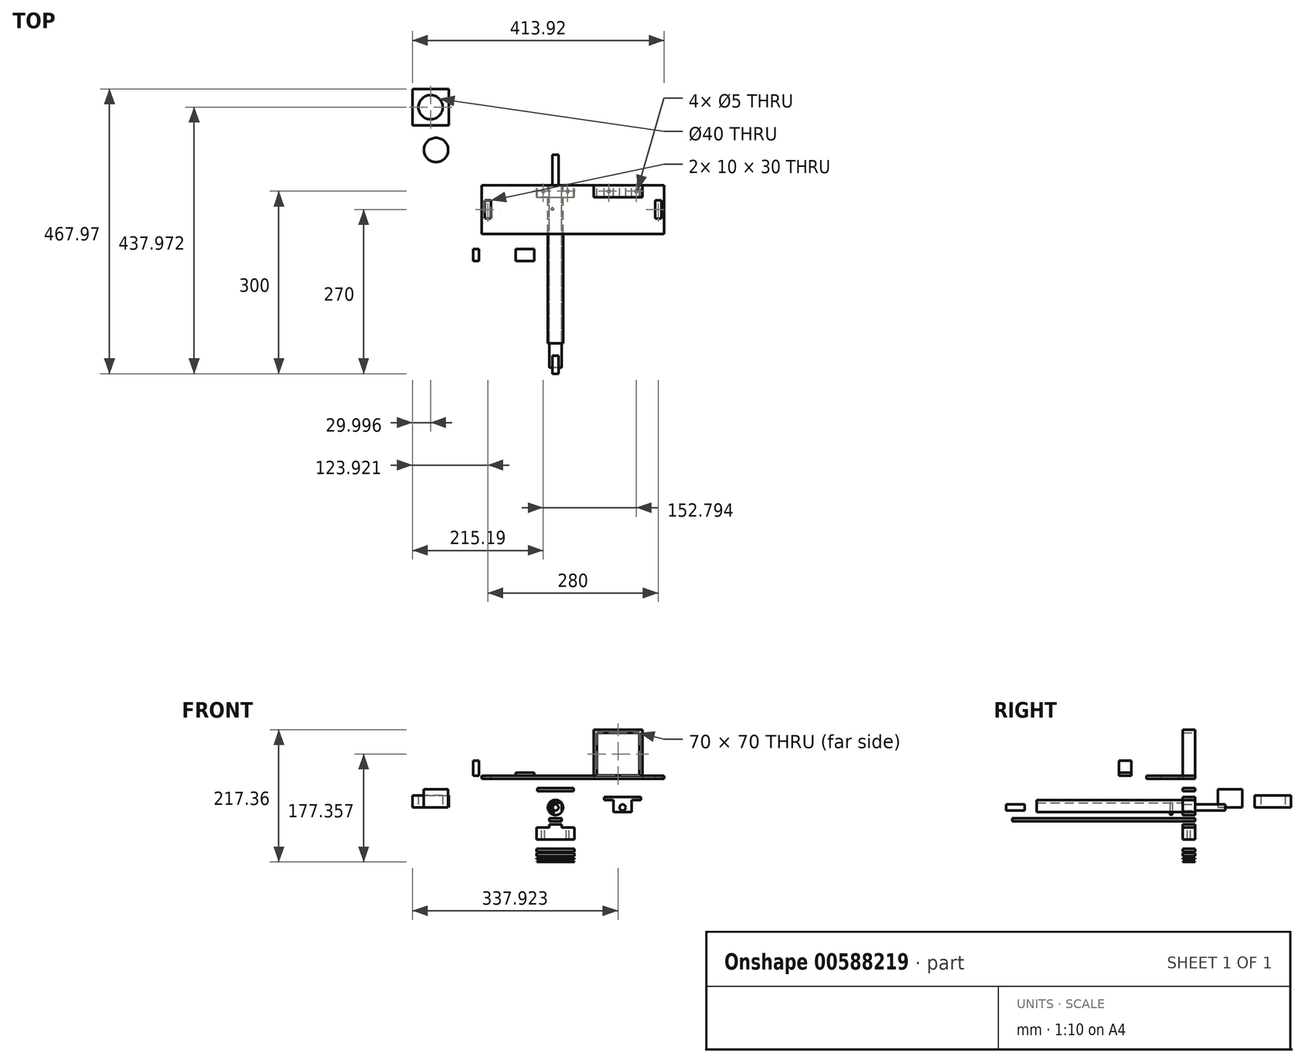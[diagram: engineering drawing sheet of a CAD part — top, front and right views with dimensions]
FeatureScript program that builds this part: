
annotation { "Feature Type Name" : "Feature", "Feature Type Description" : "" }
export const myFeature = defineFeature(function(context is Context, id is Id, definition is map)
    precondition{}
    {
        {
            var Q0;
            Q0=qCreatedBy(makeId("Front.planeOp"),FACE);
            var sketch = newSketch(context, id + "F0", { "sketchPlane" : qUnion([Q0])});
            skCircle(sketch, "E0", {"center": v(0, 0) * mm, "radius": 12.5 * mm});
            skCircle(sketch, "E1", {"center": v(110.3, 0) * mm, "radius": 5 * mm});
            skLineSegment(sketch, "E2.bottom", {"start": v(-30, 31.74) * mm, "end": v(30, 31.74) * mm});
            skLineSegment(sketch, "E2.top", {"start": v(-30, 26.74) * mm, "end": v(30, 26.74) * mm});
            skLineSegment(sketch, "E2.left", {"start": v(-30, 31.74) * mm, "end": v(-30, 26.74) * mm});
            skLineSegment(sketch, "E2.right", {"start": v(30, 31.74) * mm, "end": v(30, 26.74) * mm});
            skPoint(sketch, "E2.middle", {"position": v(0, 29.24) * mm});
            skLineSegment(sketch, "E3", {"start": v(110.3, 10) * mm, "end": v(110.3, -10) * mm, "construction": true});
            skCircle(sketch, "E4", {"center": v(110.3, 0) * mm, "radius": 12.5 * mm, "construction": true});
            skLineSegment(sketch, "E5", {"start": v(97.8, 0) * mm, "end": v(122.8, 0) * mm, "construction": true});
            skLineSegment(sketch, "E6", {"start": v(110.3, 12.5) * mm, "end": v(79.29, 12.5) * mm, "construction": true});
            skLineSegment(sketch, "E7", {"start": v(110.3, 5) * mm, "end": v(79.29, 5) * mm, "construction": true});
            skLineSegment(sketch, "E8", {"start": v(110.3, -5) * mm, "end": v(79.29, -5) * mm, "construction": true});
            skLineSegment(sketch, "E9", {"start": v(110.3, -12.5) * mm, "end": v(79.29, -12.5) * mm, "construction": true});
            skLineSegment(sketch, "E10", {"start": v(110.3, -7.5) * mm, "end": v(125.3, -7.5) * mm});
            skLineSegment(sketch, "E11", {"start": v(110.3, 17.5) * mm, "end": v(140.3, 17.5) * mm});
            skLineSegment(sketch, "E12", {"start": v(125.3, 12.5) * mm, "end": v(140.3, 12.5) * mm});
            skLineSegment(sketch, "E13", {"start": v(125.3, -7.5) * mm, "end": v(125.3, 12.5) * mm});
            skLineSegment(sketch, "E14", {"start": v(140.3, 17.5) * mm, "end": v(140.3, 12.5) * mm});
            skPoint(sketch, "E15.orphan", {"position": v(110.3, 12.5) * mm});
            skLineSegment(sketch, "E16.MirrorCS", {"start": v(95.3, 12.5) * mm, "end": v(80.3, 12.5) * mm});
            skLineSegment(sketch, "E17.MirrorCS", {"start": v(80.3, 17.5) * mm, "end": v(80.3, 12.5) * mm});
            skLineSegment(sketch, "E18.MirrorCS", {"start": v(110.3, 17.5) * mm, "end": v(80.3, 17.5) * mm});
            skLineSegment(sketch, "E19.MirrorCS", {"start": v(95.3, -7.5) * mm, "end": v(95.3, 12.5) * mm});
            skLineSegment(sketch, "E20.MirrorCS", {"start": v(110.3, -7.5) * mm, "end": v(95.3, -7.5) * mm});
            skLineSegment(sketch, "E21.top", {"start": v(0, -27.58) * mm, "end": v(10, -27.58) * mm});
            skLineSegment(sketch, "E22", {"start": v(10.93, -32.58) * mm, "end": v(30.93, -32.58) * mm});
            skLineSegment(sketch, "E23", {"start": v(30.93, -32.58) * mm, "end": v(30.93, -52.58) * mm});
            skLineSegment(sketch, "E24", {"start": v(30.93, -52.58) * mm, "end": v(0, -52.58) * mm});
            skLineSegment(sketch, "E25.MirrorCS", {"start": v(0, -27.58) * mm, "end": v(-10, -27.58) * mm});
            skLineSegment(sketch, "E26.MirrorCS", {"start": v(-10.93, -32.58) * mm, "end": v(-30.93, -32.58) * mm});
            skLineSegment(sketch, "E27.MirrorCS", {"start": v(-30.93, -32.58) * mm, "end": v(-30.93, -52.58) * mm});
            skLineSegment(sketch, "E28.MirrorCS", {"start": v(-30.93, -52.58) * mm, "end": v(0, -52.58) * mm});
            skLineSegment(sketch, "E29", {"start": v(0, -22.52) * mm, "end": v(10, -22.52) * mm});
            skLineSegment(sketch, "E30", {"start": v(10, -22.52) * mm, "end": v(10, -17.52) * mm});
            skLineSegment(sketch, "E31", {"start": v(10, -17.52) * mm, "end": v(0, -17.52) * mm});
            skLineSegment(sketch, "E32.MirrorCS", {"start": v(-10, -17.52) * mm, "end": v(0, -17.52) * mm});
            skLineSegment(sketch, "E33.MirrorCS", {"start": v(0, -22.52) * mm, "end": v(-10, -22.52) * mm});
            skLineSegment(sketch, "E34.MirrorCS", {"start": v(-10, -22.52) * mm, "end": v(-10, -17.52) * mm});
            skLineSegment(sketch, "E35.bottom", {"start": v(137.73, 52.7) * mm, "end": v(67.73, 52.7) * mm});
            skLineSegment(sketch, "E35.top", {"start": v(137.73, 122.7) * mm, "end": v(67.73, 122.7) * mm});
            skLineSegment(sketch, "E35.left", {"start": v(137.73, 52.7) * mm, "end": v(137.73, 122.7) * mm});
            skLineSegment(sketch, "E35.right", {"start": v(67.73, 52.7) * mm, "end": v(67.73, 122.7) * mm});
            skPoint(sketch, "E35.middle", {"position": v(102.73, 87.7) * mm});
            skLineSegment(sketch, "E36.bottom", {"start": v(62.73, 127.7) * mm, "end": v(142.73, 127.7) * mm});
            skLineSegment(sketch, "E36.top", {"start": v(62.73, 47.7) * mm, "end": v(142.73, 47.7) * mm});
            skLineSegment(sketch, "E36.left", {"start": v(62.73, 127.7) * mm, "end": v(62.73, 47.7) * mm});
            skLineSegment(sketch, "E36.right", {"start": v(142.73, 127.7) * mm, "end": v(142.73, 47.7) * mm});
            skLineSegment(sketch, "E37.bottom", {"start": v(-30.93, -79.86) * mm, "end": v(30.93, -79.86) * mm});
            skLineSegment(sketch, "E37.top", {"start": v(-30.93, -74.86) * mm, "end": v(30.93, -74.86) * mm});
            skLineSegment(sketch, "E37.left", {"start": v(-30.93, -79.86) * mm, "end": v(-30.93, -74.86) * mm});
            skLineSegment(sketch, "E37.right", {"start": v(30.93, -79.86) * mm, "end": v(30.93, -74.86) * mm});
            skLineSegment(sketch, "E38.MirrorCS", {"start": v(-30.74, -88.65) * mm, "end": v(31.12, -88.65) * mm});
            skLineSegment(sketch, "E39.MirrorCS", {"start": v(-30.74, -89.65) * mm, "end": v(31.12, -89.65) * mm});
            skLineSegment(sketch, "E40", {"start": v(-30.93, -82.76) * mm, "end": v(30.93, -82.76) * mm});
            skLineSegment(sketch, "E41", {"start": v(30.93, -82.76) * mm, "end": v(30.93, -84.76) * mm});
            skLineSegment(sketch, "E42", {"start": v(30.93, -84.76) * mm, "end": v(-30.93, -84.76) * mm});
            skLineSegment(sketch, "E43", {"start": v(-30.93, -84.76) * mm, "end": v(-30.93, -82.76) * mm});
            skLineSegment(sketch, "E44", {"start": v(-30.74, -88.65) * mm, "end": v(-30.74, -89.65) * mm});
            skLineSegment(sketch, "E45", {"start": v(31.12, -88.65) * mm, "end": v(31.12, -89.65) * mm});
            skLineSegment(sketch, "E46", {"start": v(-30.93, -72.74) * mm, "end": v(30.93, -72.74) * mm});
            skLineSegment(sketch, "E47", {"start": v(30.93, -72.74) * mm, "end": v(30.93, -67.74) * mm});
            skLineSegment(sketch, "E48", {"start": v(30.93, -67.74) * mm, "end": v(-30.93, -67.74) * mm});
            skLineSegment(sketch, "E49", {"start": v(-30.93, -67.74) * mm, "end": v(-30.93, -72.74) * mm});
            skLineSegment(sketch, "E50", {"start": v(-10, -27.58) * mm, "end": v(-10, -32.58) * mm});
            skLineSegment(sketch, "E51", {"start": v(-10, -32.58) * mm, "end": v(-10.93, -32.58) * mm});
            skPoint(sketch, "E52.MirrorCS.end.orphan", {"position": v(-10, -27.58) * mm});
            skPoint(sketch, "E52.MirrorCS.start.orphan", {"position": v(-10.93, -32.58) * mm});
            skLineSegment(sketch, "E53", {"start": v(10, -27.58) * mm, "end": v(10, -32.58) * mm});
            skLineSegment(sketch, "E54", {"start": v(10, -32.58) * mm, "end": v(10.93, -32.58) * mm});
            skLineSegment(sketch, "E55.left", {"start": v(194.47, 95.4) * mm, "end": v(194.47, 97.9) * mm});
            skLineSegment(sketch, "E56.bottom", {"start": v(-122.7, 157) * mm, "end": v(-422.7, 157) * mm});
            skLineSegment(sketch, "E56.top", {"start": v(-122.7, 159.5) * mm, "end": v(-422.7, 159.5) * mm});
            skLineSegment(sketch, "E56.left", {"start": v(-122.7, 157) * mm, "end": v(-122.7, 159.5) * mm});
            skLineSegment(sketch, "E56.right", {"start": v(-422.7, 157) * mm, "end": v(-422.7, 159.5) * mm});
            skLineSegment(sketch, "E57", {"start": v(-272.7, 150) * mm, "end": v(-272.7, 153.49) * mm, "construction": true});
            skPoint(sketch, "E57.startSnap0", {"position": v(-272.7, 157) * mm});
            skSolve(sketch);
        }
        {
            var Q0;
            Q0=makeQuery(id+"F0.imprint","IMPRINT",FACE,{"disambiguationData":[TD([[makeQuery(id+"F0.imprint","IMPRINT",EDGE,{"derivedFrom":sQuery(id+"F0.wireOp",EDGE,"E1")}),-1.0]])]});
            var Q1;
            Q1=makeQuery(id+"F0.imprint","IMPRINT",FACE,{"disambiguationData":[TD([[makeQuery(id+"F0.imprint","IMPRINT",EDGE,{"derivedFrom":sQuery(id+"F0.wireOp",EDGE,"E2.bottom")}),-1.0]])]});
            var Q2;
            Q2=makeQuery(id+"F0.imprint","IMPRINT",FACE,{"disambiguationData":[TD([[makeQuery(id+"F0.imprint","IMPRINT",EDGE,{"derivedFrom":sQuery(id+"F0.wireOp",EDGE,"E21.top")}),-1.0]])]});
            var Q3;
            Q3=makeQuery(id+"F0.imprint","IMPRINT",FACE,{"disambiguationData":[TD([[makeQuery(id+"F0.imprint","IMPRINT",EDGE,{"derivedFrom":sQuery(id+"F0.wireOp",EDGE,"E35.bottom")}),1.0]])]});
            var Q4;
            Q4=makeQuery(id+"F0.imprint","IMPRINT",FACE,{"disambiguationData":[TD([[makeQuery(id+"F0.imprint","IMPRINT",EDGE,{"derivedFrom":sQuery(id+"F0.wireOp",EDGE,"E37.bottom")}),1.0]])]});
            var Q5;
            Q5=makeQuery(id+"F0.imprint","IMPRINT",FACE,{"disambiguationData":[TD([[makeQuery(id+"F0.imprint","IMPRINT",EDGE,{"derivedFrom":sQuery(id+"F0.wireOp",EDGE,"E38.MirrorCS")}),-1.0]])]});
            var Q6;
            Q6=makeQuery(id+"F0.imprint","IMPRINT",FACE,{"disambiguationData":[TD([[makeQuery(id+"F0.imprint","IMPRINT",EDGE,{"derivedFrom":sQuery(id+"F0.wireOp",EDGE,"E40")}),-1.0]])]});
            var Q7;
            Q7=makeQuery(id+"F0.imprint","IMPRINT",FACE,{"disambiguationData":[TD([[makeQuery(id+"F0.imprint","IMPRINT",EDGE,{"derivedFrom":sQuery(id+"F0.wireOp",EDGE,"E46")}),1.0]])]});
            var Q8;
            {var subQ5=sQuery(id+"F0.wireOp",EDGE,"E55.right");Q8=makeQuery(id+"F0.imprint","IMPRINT",FACE,{"disambiguationData":[TD([[makeQuery(id+"F0.imprint","IMPRINT",EDGE,{"derivedFrom":subQ5}),-1.0]])]});}
            extrude(context, id + "F1", {"entities" : qUnion([Q0, Q1, Q2, Q3, Q4, Q5, Q6, Q7, Q8]), "depth" : 20 * mm, "offsetDistance" : 25 * mm});
        }
        {
            var Q0;
            Q0=makeQuery(id+"F0.imprint","IMPRINT",FACE,{"disambiguationData":[TD([[makeQuery(id+"F0.imprint","IMPRINT",EDGE,{"derivedFrom":sQuery(id+"F0.wireOp",EDGE,"E0")}),1.0]])]});
            extrude(context, id + "F2", {"entities" : qUnion([Q0]), "depth" : 260 * mm, "offsetDistance" : 25 * mm});
        }
        {
            var Q0;
            Q0=makeQuery(id+"F2.opExtrude","CAP_FACE",FACE,{"disambiguationData":[OSD([sQuery(id+"F0.wireOp",EDGE,"E0")])],"isStart":false});
            var sketch = newSketch(context, id + "F3", { "sketchPlane" : qUnion([Q0])});
            skCircle(sketch, "E58", {"center": v(0, 0) * mm, "radius": 5 * mm});
            skSolve(sketch);
        }
        {
            var Q0;
            Q0=makeQuery(id+"F3.imprint","IMPRINT",FACE,{"disambiguationData":[TD([[makeQuery(id+"F3.imprint","IMPRINT",EDGE,{"derivedFrom":sQuery(id+"F3.wireOp",EDGE,"E58")}),1.0]])]});
            extrude(context, id + "F4", {"entities" : qUnion([Q0]), "operationType" : NewBodyOperationType.ADD, "depth" : 50 * mm, "offsetDistance" : 25 * mm});
        }
        {
            var Q0;
            Q0=makeQuery(id+"F0.imprint","IMPRINT",FACE,{"disambiguationData":[TD([[makeQuery(id+"F0.imprint","IMPRINT",EDGE,{"derivedFrom":sQuery(id+"F0.wireOp",EDGE,"E29")}),1.0]])]});
            extrude(context, id + "F5", {"entities" : qUnion([Q0]), "depth" : 300 * mm, "offsetDistance" : 25 * mm});
        }
        {
            var Q0;
            Q0=makeQuery(id+"F1.opExtrude","SWEPT_FACE",FACE,{"disambiguationData":[OSD([sQuery(id+"F0.wireOp",EDGE,"E26.MirrorCS")])]});
            var sketch = newSketch(context, id + "F6", { "sketchPlane" : qUnion([Q0])});
            skCircle(sketch, "E59", {"center": v(-20, -10) * mm, "radius": 2.5 * mm});
            skSolve(sketch);
        }
        {
            var Q0;
            Q0=makeQuery(id+"F1.opExtrude","SWEPT_FACE",FACE,{"disambiguationData":[OSD([sQuery(id+"F0.wireOp",EDGE,"E22")])]});
            var sketch = newSketch(context, id + "F7", { "sketchPlane" : qUnion([Q0])});
            skCircle(sketch, "E60", {"center": v(20, -10) * mm, "radius": 2.5 * mm});
            skSolve(sketch);
        }
        {
            var Q0;
            Q0=makeQuery(id+"F6.imprint","IMPRINT",FACE,{"disambiguationData":[TD([[makeQuery(id+"F6.imprint","IMPRINT",EDGE,{"derivedFrom":sQuery(id+"F6.wireOp",EDGE,"E59")}),1.0]])]});
            var Q1;
            Q1=makeQuery(id+"F7.imprint","IMPRINT",FACE,{"disambiguationData":[TD([[makeQuery(id+"F7.imprint","IMPRINT",EDGE,{"derivedFrom":sQuery(id+"F7.wireOp",EDGE,"E60")}),1.0]])]});
            extrude(context, id + "F8", {"entities" : qUnion([Q0, Q1]), "operationType" : NewBodyOperationType.REMOVE, "oppositeDirection" : true, "depth" : 25 * mm, "offsetDistance" : 25 * mm});
        }
        {
            var Q0;
            Q0=makeQuery(id+"F1.opExtrude","SWEPT_FACE",FACE,{"disambiguationData":[OSD([sQuery(id+"F0.wireOp",EDGE,"E12")])]});
            var sketch = newSketch(context, id + "F9", { "sketchPlane" : qUnion([Q0])});
            skCircle(sketch, "E61", {"center": v(132.8, 10) * mm, "radius": 2.5 * mm});
            skPoint(sketch, "E61.centerSnap0", {"position": v(132.8, 20) * mm});
            skPoint(sketch, "E61.centerSnap1", {"position": v(125.3, 10) * mm});
            skSolve(sketch);
        }
        {
            var Q0;
            Q0=makeQuery(id+"F1.opExtrude","SWEPT_FACE",FACE,{"disambiguationData":[OSD([sQuery(id+"F0.wireOp",EDGE,"E16.MirrorCS")])]});
            var sketch = newSketch(context, id + "F10", { "sketchPlane" : qUnion([Q0])});
            skCircle(sketch, "E62", {"center": v(87.8, 10) * mm, "radius": 2.5 * mm});
            skPoint(sketch, "E62.centerSnap0", {"position": v(80.3, 10) * mm});
            skPoint(sketch, "E62.centerSnap1", {"position": v(87.8, 20) * mm});
            skSolve(sketch);
        }
        {
            var Q0;
            Q0=makeQuery(id+"F10.imprint","IMPRINT",FACE,{"disambiguationData":[TD([[makeQuery(id+"F10.imprint","IMPRINT",EDGE,{"derivedFrom":sQuery(id+"F10.wireOp",EDGE,"E62")}),1.0]])]});
            var Q1;
            Q1=makeQuery(id+"F9.imprint","IMPRINT",FACE,{"disambiguationData":[TD([[makeQuery(id+"F9.imprint","IMPRINT",EDGE,{"derivedFrom":sQuery(id+"F9.wireOp",EDGE,"E61")}),1.0]])]});
            extrude(context, id + "F11", {"entities" : qUnion([Q0, Q1]), "operationType" : NewBodyOperationType.REMOVE, "oppositeDirection" : true, "depth" : 25 * mm, "offsetDistance" : 25 * mm});
        }
        {
            var Q0;
            Q0=makeQuery(id+"F5.opExtrude","SWEPT_FACE",FACE,{"disambiguationData":[OSD([sQuery(id+"F0.wireOp",EDGE,"E31"),sQuery(id+"F0.wireOp",EDGE,"E32.MirrorCS")])]});
            var sketch = newSketch(context, id + "F12", { "sketchPlane" : qUnion([Q0])});
            skLineSegment(sketch, "E63", {"start": v(-10, -280) * mm, "end": v(10, -280) * mm});
            skCircle(sketch, "E64", {"center": v(5, -39.13) * mm, "radius": 1.93 * mm});
            skPoint(sketch, "E65.orphan", {"position": v(0, -300) * mm});
            skCircle(sketch, "E66.MirrorC", {"center": v(-5, -39.13) * mm, "radius": 1.93 * mm});
            skLineSegment(sketch, "E67", {"start": v(10, -20) * mm, "end": v(-10, -20) * mm});
            skSolve(sketch);
        }
        {
            var Q0;
            Q0=makeQuery(id+"F12.imprint","IMPRINT",FACE,{"disambiguationData":[TD([[makeQuery(id+"F12.imprint","IMPRINT",EDGE,{"derivedFrom":sQuery(id+"F12.wireOp",EDGE,"E66.MirrorC")}),-1.0]])]});
            var Q1;
            Q1=makeQuery(id+"F12.imprint","IMPRINT",FACE,{"disambiguationData":[TD([[makeQuery(id+"F12.imprint","IMPRINT",EDGE,{"derivedFrom":sQuery(id+"F12.wireOp",EDGE,"E64")}),1.0]])]});
            extrude(context, id + "F13", {"entities" : qUnion([Q0, Q1]), "operationType" : NewBodyOperationType.REMOVE, "depth" : 25 * mm, "offsetDistance" : 25 * mm});
        }
        {
            var Q0;
            Q0=makeQuery(id+"F1.opExtrude","SWEPT_FACE",FACE,{"disambiguationData":[OSD([sQuery(id+"F0.wireOp",EDGE,"E36.bottom")])]});
            var sketch = newSketch(context, id + "F14", { "sketchPlane" : qUnion([Q0])});
            skLineSegment(sketch, "E68", {"start": v(82.73, 0) * mm, "end": v(82.73, -20) * mm});
            skLineSegment(sketch, "E69", {"start": v(122.73, -20) * mm, "end": v(122.73, 0) * mm});
            skSolve(sketch);
        }
        {
            var Q0;
            Q0=makeQuery(id+"F1.opExtrude","SWEPT_FACE",FACE,{"disambiguationData":[OSD([sQuery(id+"F0.wireOp",EDGE,"E36.top")])]});
            var sketch = newSketch(context, id + "F15", { "sketchPlane" : qUnion([Q0])});
            skLineSegment(sketch, "E70", {"start": v(122.73, 20) * mm, "end": v(122.73, 0) * mm});
            skLineSegment(sketch, "E71", {"start": v(82.73, 20) * mm, "end": v(82.73, 0) * mm});
            skSolve(sketch);
        }
        {
            var Q0;
            Q0=makeQuery(id+"F2.opExtrude","CAP_FACE",FACE,{"disambiguationData":[OSD([sQuery(id+"F0.wireOp",EDGE,"E0")])],"isStart":true});
            var sketch = newSketch(context, id + "F16", { "sketchPlane" : qUnion([Q0])});
            skCircle(sketch, "E72", {"center": v(0, 0) * mm, "radius": 5 * mm});
            skSolve(sketch);
        }
        {
            var Q0;
            Q0=qSketchRegion(id+"F16",true);
            extrude(context, id + "F17", {"entities" : qUnion([Q0]), "operationType" : NewBodyOperationType.ADD, "depth" : 50 * mm, "offsetDistance" : 25 * mm});
        }
        {
            var Q0;
            Q0=qCreatedBy(makeId("Front.planeOp"),FACE);
            var sketch = newSketch(context, id + "F18", { "sketchPlane" : qUnion([Q0])});
            skLineSegment(sketch, "E73.bottom", {"start": v(-121.27, 52.06) * mm, "end": v(178.73, 52.06) * mm});
            skLineSegment(sketch, "E73.top", {"start": v(-121.27, 47.06) * mm, "end": v(178.73, 47.06) * mm});
            skLineSegment(sketch, "E73.left", {"start": v(-121.27, 52.06) * mm, "end": v(-121.27, 47.06) * mm});
            skLineSegment(sketch, "E73.right", {"start": v(178.73, 52.06) * mm, "end": v(178.73, 47.06) * mm});
            skSolve(sketch);
        }
        {
            var Q0;
            Q0=makeQuery(id+"F18.imprint","IMPRINT",FACE,{"disambiguationData":[TD([[makeQuery(id+"F18.imprint","IMPRINT",EDGE,{"derivedFrom":sQuery(id+"F18.wireOp",EDGE,"E73.bottom")}),-1.0]])]});
            extrude(context, id + "F19", {"entities" : qUnion([Q0]), "depth" : 80 * mm, "offsetDistance" : 25 * mm});
        }
        {
            var Q0;
            Q0=makeQuery(id+"F19.opExtrude","SWEPT_FACE",FACE,{"disambiguationData":[OSD([sQuery(id+"F18.wireOp",EDGE,"E73.bottom")])]});
            var sketch = newSketch(context, id + "F20", { "sketchPlane" : qUnion([Q0])});
            skLineSegment(sketch, "E74", {"start": v(-101.27, 0) * mm, "end": v(-101.27, -80) * mm});
            skLineSegment(sketch, "E75.bottom", {"start": v(-116.27, -25) * mm, "end": v(-106.27, -25) * mm});
            skLineSegment(sketch, "E75.top", {"start": v(-116.27, -55) * mm, "end": v(-106.27, -55) * mm});
            skLineSegment(sketch, "E75.left", {"start": v(-116.27, -25) * mm, "end": v(-116.27, -55) * mm});
            skLineSegment(sketch, "E75.right", {"start": v(-106.27, -25) * mm, "end": v(-106.27, -55) * mm});
            skPoint(sketch, "E75.middle", {"position": v(-111.27, -40) * mm});
            skLineSegment(sketch, "E76", {"start": v(28.73, 0) * mm, "end": v(28.73, -80) * mm, "construction": true});
            skLineSegment(sketch, "E77.MirrorCS", {"start": v(163.73, -25) * mm, "end": v(163.73, -55) * mm});
            skLineSegment(sketch, "E78.MirrorCS", {"start": v(173.73, -25) * mm, "end": v(163.73, -25) * mm});
            skLineSegment(sketch, "E79.MirrorCS", {"start": v(173.73, -25) * mm, "end": v(173.73, -55) * mm});
            skLineSegment(sketch, "E80.MirrorCS", {"start": v(173.73, -55) * mm, "end": v(163.73, -55) * mm});
            skLineSegment(sketch, "E81.MirrorCS", {"start": v(158.73, 0) * mm, "end": v(158.73, -80) * mm});
            skLineSegment(sketch, "E82.bottom", {"start": v(-65.07, -104.85) * mm, "end": v(-35.07, -104.85) * mm});
            skLineSegment(sketch, "E82.top", {"start": v(-65.07, -124.85) * mm, "end": v(-35.07, -124.85) * mm});
            skLineSegment(sketch, "E82.left", {"start": v(-65.07, -104.85) * mm, "end": v(-65.07, -124.85) * mm});
            skLineSegment(sketch, "E82.right", {"start": v(-35.07, -104.85) * mm, "end": v(-35.07, -124.85) * mm});
            skLineSegment(sketch, "E83.bottom", {"start": v(-135.53, -104.85) * mm, "end": v(-125.53, -104.85) * mm});
            skLineSegment(sketch, "E83.top", {"start": v(-135.53, -124.85) * mm, "end": v(-125.53, -124.85) * mm});
            skLineSegment(sketch, "E83.left", {"start": v(-135.53, -104.85) * mm, "end": v(-135.53, -124.85) * mm});
            skLineSegment(sketch, "E83.right", {"start": v(-125.53, -104.85) * mm, "end": v(-125.53, -124.85) * mm});
            skSolve(sketch);
        }
        {
            var Q0;
            Q0=qCreatedBy(makeId("Top.planeOp"),FACE);
            var sketch = newSketch(context, id + "F21", { "sketchPlane" : qUnion([Q0])});
            skCircle(sketch, "E84", {"center": v(-196.25, 57.8) * mm, "radius": 20 * mm});
            skLineSegment(sketch, "E85.bottom", {"start": v(-235.2, 97.97) * mm, "end": v(-175.2, 97.97) * mm});
            skLineSegment(sketch, "E85.top", {"start": v(-235.2, 157.97) * mm, "end": v(-175.2, 157.97) * mm});
            skLineSegment(sketch, "E85.left", {"start": v(-235.2, 97.97) * mm, "end": v(-235.2, 157.97) * mm});
            skLineSegment(sketch, "E85.right", {"start": v(-175.2, 97.97) * mm, "end": v(-175.2, 157.97) * mm});
            skCircle(sketch, "E86", {"center": v(-205.2, 127.97) * mm, "radius": 20 * mm});
            skPoint(sketch, "E86.centerSnap0", {"position": v(-175.2, 127.97) * mm});
            skPoint(sketch, "E86.centerSnap1", {"position": v(-205.2, 97.97) * mm});
            skSolve(sketch);
        }
        {
            var Q0;
            Q0=makeQuery(id+"F21.imprint","IMPRINT",FACE,{"disambiguationData":[TD([[makeQuery(id+"F21.imprint","IMPRINT",EDGE,{"derivedFrom":sQuery(id+"F21.wireOp",EDGE,"E84")}),1.0]])]});
            extrude(context, id + "F22", {"entities" : qUnion([Q0]), "depth" : 30 * mm, "offsetDistance" : 25 * mm});
        }
        {
            var Q0;
            Q0=makeQuery(id+"F21.imprint","IMPRINT",FACE,{"disambiguationData":[TD([[makeQuery(id+"F21.imprint","IMPRINT",EDGE,{"derivedFrom":sQuery(id+"F21.wireOp",EDGE,"E85.bottom")}),1.0]])]});
            extrude(context, id + "F23", {"entities" : qUnion([Q0]), "depth" : 20 * mm, "offsetDistance" : 25 * mm});
        }
        {
            var Q0;
            Q0=makeQuery(id+"F20.imprint","IMPRINT",FACE,{"disambiguationData":[TD([[makeQuery(id+"F20.imprint","IMPRINT",EDGE,{"derivedFrom":sQuery(id+"F20.wireOp",EDGE,"E75.bottom")}),-1.0]])]});
            var Q1;
            Q1=makeQuery(id+"F20.imprint","IMPRINT",FACE,{"disambiguationData":[TD([[makeQuery(id+"F20.imprint","IMPRINT",EDGE,{"derivedFrom":sQuery(id+"F20.wireOp",EDGE,"E77.MirrorCS")}),1.0]])]});
            extrude(context, id + "F24", {"entities" : qUnion([Q0, Q1]), "operationType" : NewBodyOperationType.REMOVE, "endBound" : BoundingType.THROUGH_ALL, "oppositeDirection" : true, "depth" : 25 * mm, "offsetDistance" : 25 * mm});
        }
        {
            var Q0;
            Q0=makeQuery(id+"F20.imprint","IMPRINT",FACE,{"disambiguationData":[TD([[makeQuery(id+"F20.imprint","IMPRINT",EDGE,{"derivedFrom":sQuery(id+"F20.wireOp",EDGE,"E83.bottom")}),-1.0]])]});
            extrude(context, id + "F25", {"entities" : qUnion([Q0]), "depth" : 25 * mm, "offsetDistance" : 25 * mm});
        }
        {
            var Q0;
            Q0=makeQuery(id+"F20.imprint","IMPRINT",FACE,{"disambiguationData":[TD([[makeQuery(id+"F20.imprint","IMPRINT",EDGE,{"derivedFrom":sQuery(id+"F20.wireOp",EDGE,"E82.bottom")}),-1.0]])]});
            extrude(context, id + "F26", {"entities" : qUnion([Q0]), "depth" : 5 * mm, "offsetDistance" : 25 * mm});
        }
    });
